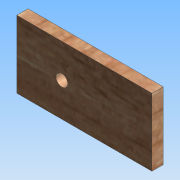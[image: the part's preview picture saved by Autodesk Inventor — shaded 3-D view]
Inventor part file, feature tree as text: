
AUTODESK INVENTOR PART (.ipt)
format: ipt  version: 2015 (Build 190159000, 159)  size: 113,664 bytes
history: native  units: mm
features: extrude x2, sketch x2, projected_geometry x1
ambient origin geometry x8: Origin, YZ Plane, XZ Plane, XY Plane, X Axis, Y Axis, Z Axis, Center Point
bodies: Body1 (feature_tree)
feature tree (5):
  extrude  "Extrusion2"  Depth=80.0mm
  extrude  "Extrusion3"  Depth=5.0mm TaperAngle=0.0deg
  sketch  "Sketch1"  dims[d2=30.0mm d3=80.0mm]
  sketch  "Sketch3"  dims[d4=5.2mm d5=5.0mm d6=0.0mm d7=15.0mm d8=15.0mm d11=10.0mm d12=10.0mm d14=10.0mm d15=0.0mm d17=64.5mm]
  projected_geometry  "Projected Loop1"
